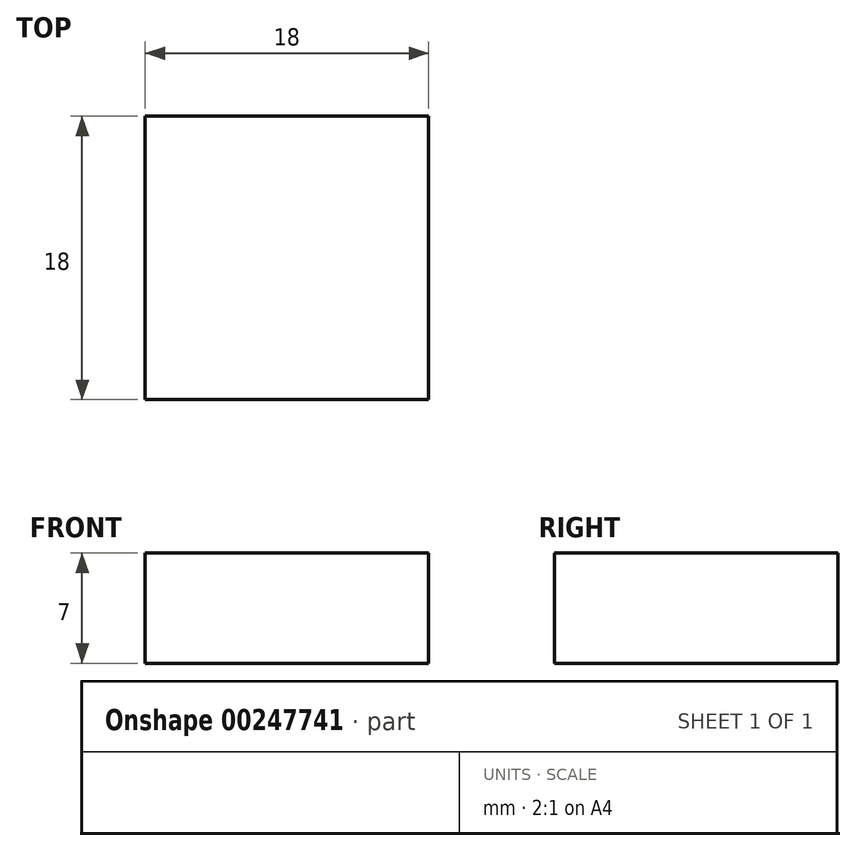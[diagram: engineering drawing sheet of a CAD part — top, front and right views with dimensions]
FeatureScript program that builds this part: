
annotation { "Feature Type Name" : "Feature", "Feature Type Description" : "" }
export const myFeature = defineFeature(function(context is Context, id is Id, definition is map)
    precondition{}
    {
        {
            var Q0;
            Q0=qCreatedBy(makeId("Top.planeOp"),FACE);
            var sketch = newSketch(context, id + "F0", { "sketchPlane" : qUnion([Q0])});
            skLineSegment(sketch, "E0.bottom", {"start": v(9, -9) * mm, "end": v(-9, -9) * mm});
            skLineSegment(sketch, "E0.top", {"start": v(9, 9) * mm, "end": v(-9, 9) * mm});
            skLineSegment(sketch, "E0.left", {"start": v(9, -9) * mm, "end": v(9, 9) * mm});
            skLineSegment(sketch, "E0.right", {"start": v(-9, -9) * mm, "end": v(-9, 9) * mm});
            skPoint(sketch, "E0.middle", {"position": v(0, 0) * mm});
            skSolve(sketch);
        }
        {
            var Q0;
            Q0 = qSketchRegion(id + "F0", true);
            extrude(context, id + "F1", {"entities" : qUnion([Q0]), "depth" : 7 * mm});
        }
    });
